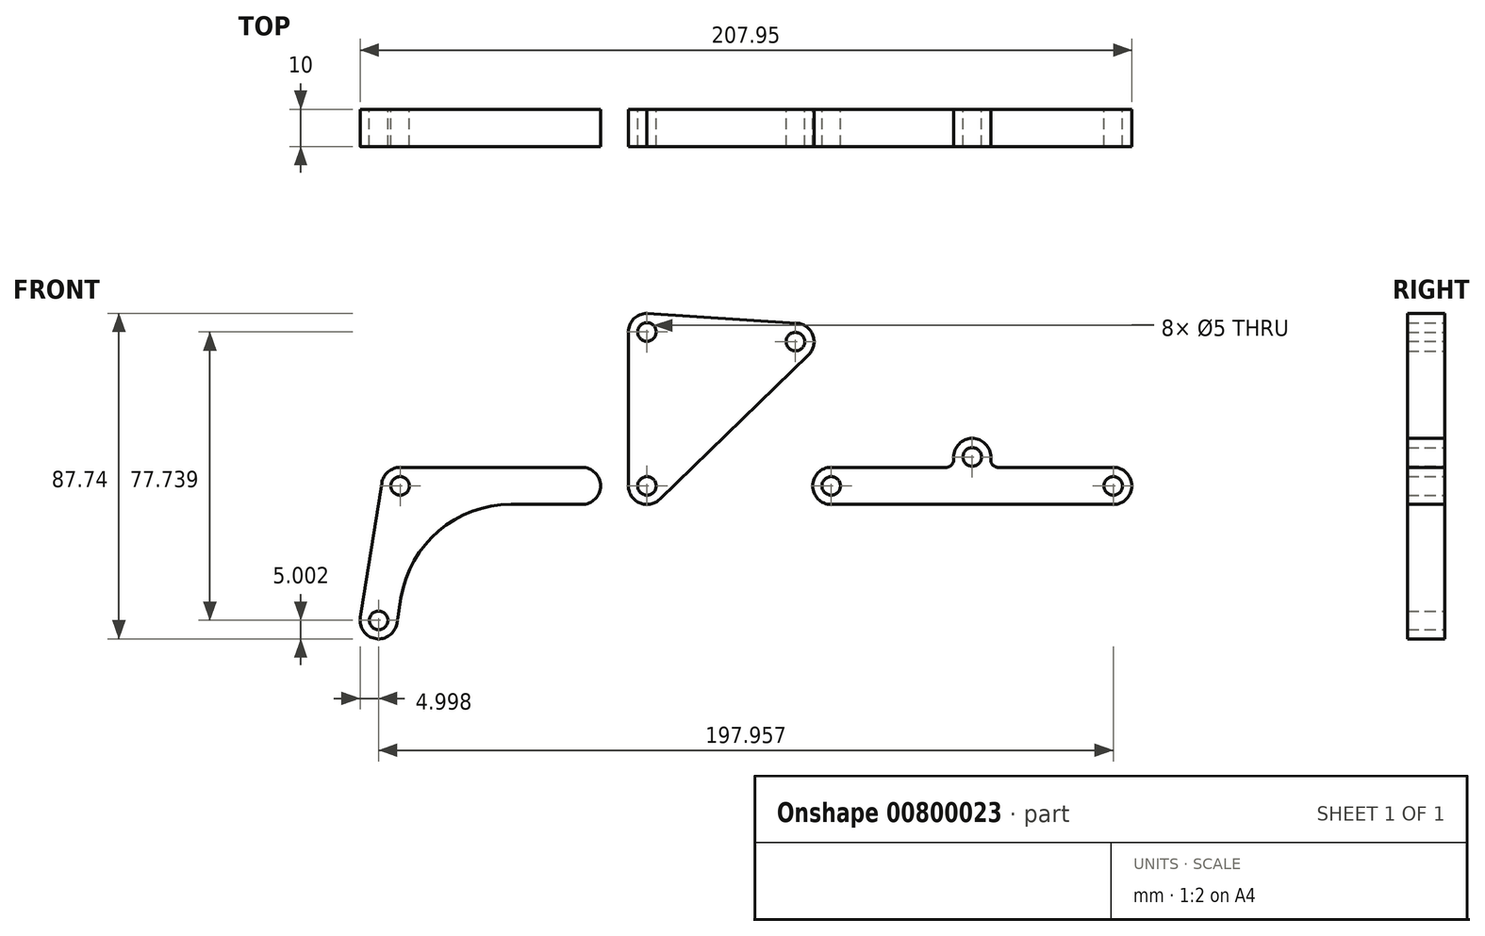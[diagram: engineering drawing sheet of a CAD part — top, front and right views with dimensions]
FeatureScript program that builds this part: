
annotation { "Feature Type Name" : "Feature", "Feature Type Description" : "" }
export const myFeature = defineFeature(function(context is Context, id is Id, definition is map)
    precondition{}
    {
        {
            var Q0;
            Q0=qCreatedBy(makeId("Front.planeOp"),FACE);
            var sketch = newSketch(context, id + "F0", { "sketchPlane" : qUnion([Q0])});
            skArc(sketch, "E0", {"start": v(0.65, 46.46) * mm, "mid": v(-3.3, 45.26) * mm, "end": v(-5, 41.5) * mm});
            skArc(sketch, "E1", {"start": v(-5, 0) * mm, "mid": v(-1.95, -4.6) * mm, "end": v(3.48, -3.59) * mm});
            skArc(sketch, "E2", {"start": v(43.5, 35.3) * mm, "mid": v(44.7, 40.62) * mm, "end": v(40.34, 43.88) * mm});
            skLineSegment(sketch, "E3", {"start": v(0, 46.5) * mm, "end": v(40.34, 43.88) * mm});
            skLineSegment(sketch, "E4", {"start": v(-5, 41.5) * mm, "end": v(-5, 0) * mm});
            skLineSegment(sketch, "E5", {"start": v(43.5, 35.3) * mm, "end": v(3.48, -3.59) * mm});
            skCircle(sketch, "E6", {"center": v(0, 41.5) * mm, "radius": 2.5 * mm});
            skCircle(sketch, "E7", {"center": v(0, 0) * mm, "radius": 2.5 * mm});
            skCircle(sketch, "E8", {"center": v(40.01, 38.9) * mm, "radius": 2.5 * mm});
            skSolve(sketch);
        }
        {
            var Q0;
            Q0=makeQuery(id+"F0.imprint","IMPRINT",FACE,{"disambiguationData":[TD([[makeQuery(id+"F0.imprint","IMPRINT",EDGE,{"derivedFrom":sQuery(id+"F0.wireOp",EDGE,"E1")}),1.0]])]});
            extrude(context, id + "F1", {"entities" : qUnion([Q0]), "depth" : 10 * mm, "offsetDistance" : 25 * mm});
        }
        {
            var Q0;
            Q0=qCreatedBy(makeId("Front.planeOp"),FACE);
            var sketch = newSketch(context, id + "F2", { "sketchPlane" : qUnion([Q0])});
            skArc(sketch, "E9", {"start": v(-17.5, -5) * mm, "mid": v(-12.5, 0) * mm, "end": v(-17.5, 5) * mm});
            skArc(sketch, "E10", {"start": v(-77.24, -35.45) * mm, "mid": v(-73.1, -41.18) * mm, "end": v(-67.36, -37.03) * mm});
            skLineSegment(sketch, "E11", {"start": v(-77.24, -35.45) * mm, "end": v(-71.44, 0.8) * mm});
            skLineSegment(sketch, "E12", {"start": v(-66.5, 5) * mm, "end": v(-17.5, 5) * mm});
            skLineSegment(sketch, "E13", {"start": v(-67.36, -37.03) * mm, "end": v(-66.28, -30.26) * mm});
            skLineSegment(sketch, "E14", {"start": v(-17.5, -5) * mm, "end": v(-36.66, -5) * mm});
            skPoint(sketch, "E15.visualSharp", {"position": v(-62.24, -5) * mm});
            skArc(sketch, "E15.filletArc", {"start": v(-36.66, -5) * mm, "mid": v(-56.12, -12.17) * mm, "end": v(-66.28, -30.26) * mm});
            skCircle(sketch, "E16", {"center": v(-66.5, 0) * mm, "radius": 2.5 * mm});
            skCircle(sketch, "E17", {"center": v(-72.3, -36.24) * mm, "radius": 2.5 * mm});
            skArc(sketch, "E18", {"start": v(-66.5, 5) * mm, "mid": v(-69.74, 3.8) * mm, "end": v(-71.44, 0.8) * mm});
            skPoint(sketch, "E19.orphan", {"position": v(-71.56, 0) * mm});
            skSolve(sketch);
        }
        {
            var Q0;
            Q0=qCreatedBy(makeId("Front.planeOp"),FACE);
            var sketch = newSketch(context, id + "F3", { "sketchPlane" : qUnion([Q0])});
            skArc(sketch, "E20", {"start": v(49.65, 5) * mm, "mid": v(44.65, 0) * mm, "end": v(49.65, -5) * mm});
            skArc(sketch, "E21", {"start": v(92.65, 7.8) * mm, "mid": v(87.65, 12.8) * mm, "end": v(82.65, 7.8) * mm});
            skLineSegment(sketch, "E22", {"start": v(49.65, -5) * mm, "end": v(87.65, -5) * mm});
            skLineSegment(sketch, "E23", {"start": v(92.65, 7.8) * mm, "end": v(92.65, 7) * mm});
            skLineSegment(sketch, "E24", {"start": v(49.65, 5) * mm, "end": v(80.65, 5) * mm});
            skLineSegment(sketch, "E25", {"start": v(82.65, 7.8) * mm, "end": v(82.65, 7) * mm});
            skPoint(sketch, "E26.visualSharp", {"position": v(92.65, -5) * mm});
            skPoint(sketch, "E27.visualSharp", {"position": v(82.65, 5) * mm});
            skArc(sketch, "E27.filletArc", {"start": v(80.65, 5) * mm, "mid": v(82.07, 5.59) * mm, "end": v(82.65, 7) * mm});
            skCircle(sketch, "E28", {"center": v(49.65, 0) * mm, "radius": 2.5 * mm});
            skCircle(sketch, "E29", {"center": v(87.65, 7.8) * mm, "radius": 2.5 * mm});
            skLineSegment(sketch, "E30", {"start": v(87.65, 18.97) * mm, "end": v(87.65, -13) * mm, "construction": true});
            skArc(sketch, "E31.MirrorCS", {"start": v(94.65, 5) * mm, "mid": v(93.24, 5.59) * mm, "end": v(92.65, 7) * mm});
            skArc(sketch, "E32.MirrorCS", {"start": v(82.65, 7.8) * mm, "mid": v(87.65, 12.8) * mm, "end": v(92.65, 7.8) * mm});
            skLineSegment(sketch, "E33.MirrorCS", {"start": v(125.65, -5) * mm, "end": v(87.65, -5) * mm});
            skLineSegment(sketch, "E34.MirrorCS", {"start": v(125.65, 5) * mm, "end": v(94.65, 5) * mm});
            skCircle(sketch, "E35.MirrorC", {"center": v(125.65, 0) * mm, "radius": 2.5 * mm});
            skPoint(sketch, "E36.MirrorP", {"position": v(92.65, 5) * mm});
            skArc(sketch, "E37.MirrorCS", {"start": v(125.65, 5) * mm, "mid": v(130.65, 0) * mm, "end": v(125.65, -5) * mm});
            skSolve(sketch);
        }
        {
            var Q0;
            Q0=makeQuery(id+"F2.imprint","IMPRINT",FACE,{"disambiguationData":[TD([[makeQuery(id+"F2.imprint","IMPRINT",EDGE,{"derivedFrom":sQuery(id+"F2.wireOp",EDGE,"E9")}),1.0]])]});
            extrude(context, id + "F4", {"entities" : qUnion([Q0]), "depth" : 10 * mm, "offsetDistance" : 25 * mm});
        }
        {
            var Q0;
            Q0=makeQuery(id+"F3.imprint","IMPRINT",FACE,{"disambiguationData":[TD([[makeQuery(id+"F3.imprint","IMPRINT",EDGE,{"derivedFrom":sQuery(id+"F3.wireOp",EDGE,"E20")}),1.0]])]});
            extrude(context, id + "F5", {"entities" : qUnion([Q0]), "depth" : 10 * mm, "offsetDistance" : 25 * mm});
        }
    });
